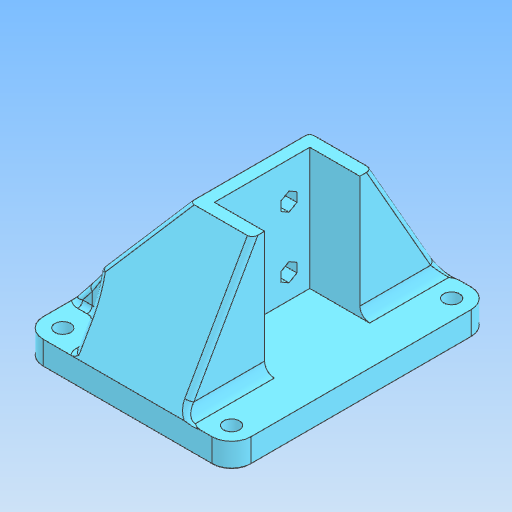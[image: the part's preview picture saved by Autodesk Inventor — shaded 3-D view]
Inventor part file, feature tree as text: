
AUTODESK INVENTOR PART (.ipt)
format: ipt  version: 2021.2 (Build 252289000, 289)  size: 433,152 bytes
history: native  units: mm
features: other x4, fillet x4, chamfer x1
ambient origin geometry x8: Origin, YZ Plane, XZ Plane, XY Plane, X Axis, Y Axis, Z Axis, Center Point
bodies: Body1 (feature_tree)
feature tree (9):
  other  "Твёрдое тело.ipt"
  fillet  "Сопряжение1"  Radius=10.0mm
  fillet  "Сопряжение2"  Radius=8.0mm
  fillet  "Сопряжение3"  Radius=4.0mm
  fillet  "Сопряжение4"  Radius=2.0mm
  chamfer  "Фаска1"  Distance=2.0mm
  other  "Фланец::Твёрдое тело.ipt"
  other  "Элемент создания тегов1"
  other  "Твердое тело1"
